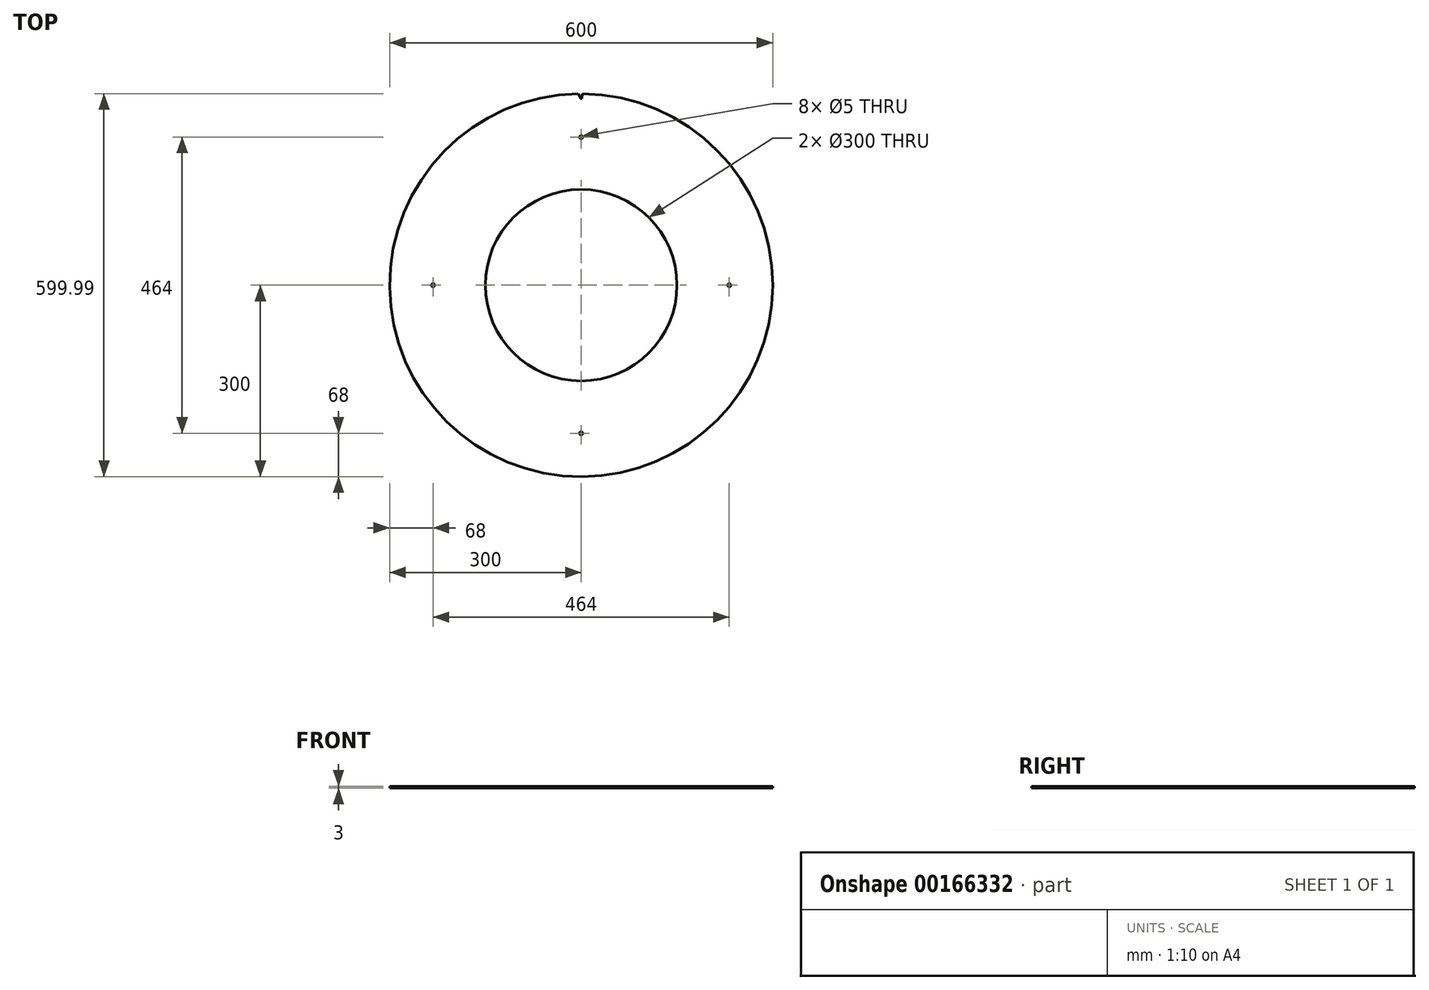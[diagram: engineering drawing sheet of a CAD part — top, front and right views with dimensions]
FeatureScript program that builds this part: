
annotation { "Feature Type Name" : "Feature", "Feature Type Description" : "" }
export const myFeature = defineFeature(function(context is Context, id is Id, definition is map)
    precondition{}
    {
        {
            var Q0;
            Q0=qCreatedBy(makeId("Top.planeOp"),FACE);
            var sketch = newSketch(context, id + "F0", { "sketchPlane" : qUnion([Q0])});
            skCircle(sketch, "E0", {"center": v(0, 0) * mm, "radius": 300 * mm});
            skCircle(sketch, "E1", {"center": v(0, 0) * mm, "radius": 150 * mm});
            skSolve(sketch);
        }
        {
            var Q0;
            Q0=makeQuery(id+"F0.imprint","IMPRINT",FACE,{"disambiguationData":[TD([[makeQuery(id+"F0.imprint","IMPRINT",EDGE,{"derivedFrom":sQuery(id+"F0.wireOp",EDGE,"E0")}),1.0]])]});
            extrude(context, id + "F1", {"entities" : qUnion([Q0]), "depth" : 3 * mm});
        }
        {
            var Q0;
            Q0=makeQuery(id+"F1.opExtrude","CAP_FACE",FACE,{"disambiguationData":[OSD([sQuery(id+"F0.wireOp",EDGE,"E0"),sQuery(id+"F0.wireOp",EDGE,"E1")])],"isStart":false});
            var sketch = newSketch(context, id + "F2", { "sketchPlane" : qUnion([Q0])});
            skCircle(sketch, "E2", {"center": v(0, 232) * mm, "radius": 2.5 * mm});
            skLineSegment(sketch, "E3", {"start": v(0, 0) * mm, "end": v(0, 232) * mm});
            skCircle(sketch, "E4.1.0", {"center": v(-232, 0) * mm, "radius": 2.5 * mm});
            skCircle(sketch, "E4.2.0", {"center": v(0, -232) * mm, "radius": 2.5 * mm});
            skCircle(sketch, "E4.3.0", {"center": v(232, 0) * mm, "radius": 2.5 * mm});
            skPoint(sketch, "E4.center", {"position": v(0, 0) * mm});
            skSolve(sketch);
        }
        {
            var Q0;
            Q0=qSketchRegion(id+"F2",true);
            extrude(context, id + "F3", {"entities" : qUnion([Q0]), "operationType" : NewBodyOperationType.REMOVE, "oppositeDirection" : true, "depth" : 3 * mm});
        }
        {
            var Q0;
            Q0=makeQuery(id+"F1.opExtrude","CAP_FACE",FACE,{"disambiguationData":[OSD([sQuery(id+"F0.wireOp",EDGE,"E0"),sQuery(id+"F0.wireOp",EDGE,"E1")])],"isStart":false});
            var sketch = newSketch(context, id + "F4", { "sketchPlane" : qUnion([Q0])});
            skLineSegment(sketch, "E5", {"start": v(0, 0) * mm, "end": v(0, 292.85) * mm});
            skCircle(sketch, "E6", {"center": v(0, 292.85) * mm, "radius": 0.55 * mm});
            skLineSegment(sketch, "E7", {"start": v(0, 0) * mm, "end": v(-2, 292.84) * mm});
            skLineSegment(sketch, "E8", {"start": v(0, 0) * mm, "end": v(2, 292.84) * mm});
            skLineSegment(sketch, "E9", {"start": v(-2, 292.84) * mm, "end": v(0, 292.85) * mm});
            skLineSegment(sketch, "E10", {"start": v(0, 292.85) * mm, "end": v(2, 292.84) * mm});
            skLineSegment(sketch, "E11", {"start": v(-1, 292.84) * mm, "end": v(0, 0) * mm});
            skLineSegment(sketch, "E12", {"start": v(0, 0) * mm, "end": v(1, 292.84) * mm});
            skLineSegment(sketch, "E13", {"start": v(2.22, 302.68) * mm, "end": v(-5.48, 302.84) * mm});
            skLineSegment(sketch, "E14", {"start": v(2.22, 302.68) * mm, "end": v(1, 292.84) * mm});
            skLineSegment(sketch, "E15", {"start": v(-5.48, 302.84) * mm, "end": v(-1, 292.84) * mm});
            skSolve(sketch);
        }
        {
            var Q0;
            {var subQ0=sQuery(id+"F4.wireOp",EDGE,"E13");Q0=makeQuery(id+"F4.imprint","IMPRINT",FACE,{"disambiguationData":[TD([[makeQuery(id+"F4.imprint","IMPRINT",EDGE,{"derivedFrom":subQ0}),1.0]])]});}
            var Q1;
            {var subQ5=sQuery(id+"F4.wireOp",EDGE,"E6");var subQ8=sQuery(id+"F4.wireOp",EDGE,"E9");var subQ11=makeQuery(id+"F4.imprint","INTERSECT",VERTEX,{"derivedFrom":[subQ5,subQ8]});Q1=makeQuery(id+"F4.imprint","IMPRINT",FACE,{"disambiguationData":[TD([[makeQuery(id+"F4.imprint","IMPRINT",EDGE,{"disambiguationData":[TD([[subQ11,1.0]])],"derivedFrom":subQ5}),-1.0]])]});}
            var Q2;
            {var subQ0=sQuery(id+"F4.wireOp",EDGE,"E9");var subQ1=sQuery(id+"F4.wireOp",EDGE,"E6");var subQ2=makeQuery(id+"F4.imprint","INTERSECT",VERTEX,{"derivedFrom":[subQ1,subQ0]});Q2=makeQuery(id+"F4.imprint","IMPRINT",FACE,{"disambiguationData":[TD([[makeQuery(id+"F4.imprint","IMPRINT",EDGE,{"disambiguationData":[TD([[subQ2,1.0]])],"derivedFrom":subQ1}),1.0]])]});}
            var Q3;
            {var subQ1=sQuery(id+"F4.wireOp",EDGE,"E5");var subQ3=sQuery(id+"F4.wireOp",EDGE,"E6");var subQ4=makeQuery(id+"F4.imprint","INTERSECT",VERTEX,{"derivedFrom":[subQ1,subQ3]});Q3=makeQuery(id+"F4.imprint","IMPRINT",FACE,{"disambiguationData":[TD([[makeQuery(id+"F4.imprint","IMPRINT",EDGE,{"disambiguationData":[TD([[subQ4,1.0]])],"derivedFrom":subQ3}),1.0]])]});}
            var Q4;
            {var subQ1=sQuery(id+"F4.wireOp",EDGE,"E5");var subQ3=sQuery(id+"F4.wireOp",EDGE,"E6");var subQ4=makeQuery(id+"F4.imprint","INTERSECT",VERTEX,{"derivedFrom":[subQ1,subQ3]});Q4=makeQuery(id+"F4.imprint","IMPRINT",FACE,{"disambiguationData":[TD([[makeQuery(id+"F4.imprint","IMPRINT",EDGE,{"disambiguationData":[TD([[subQ4,-1.0]])],"derivedFrom":subQ3}),1.0]])]});}
            extrude(context, id + "F5", {"entities" : qUnion([Q0, Q1, Q2, Q3, Q4]), "operationType" : NewBodyOperationType.REMOVE, "oppositeDirection" : true, "depth" : 3 * mm});
        }
    });
